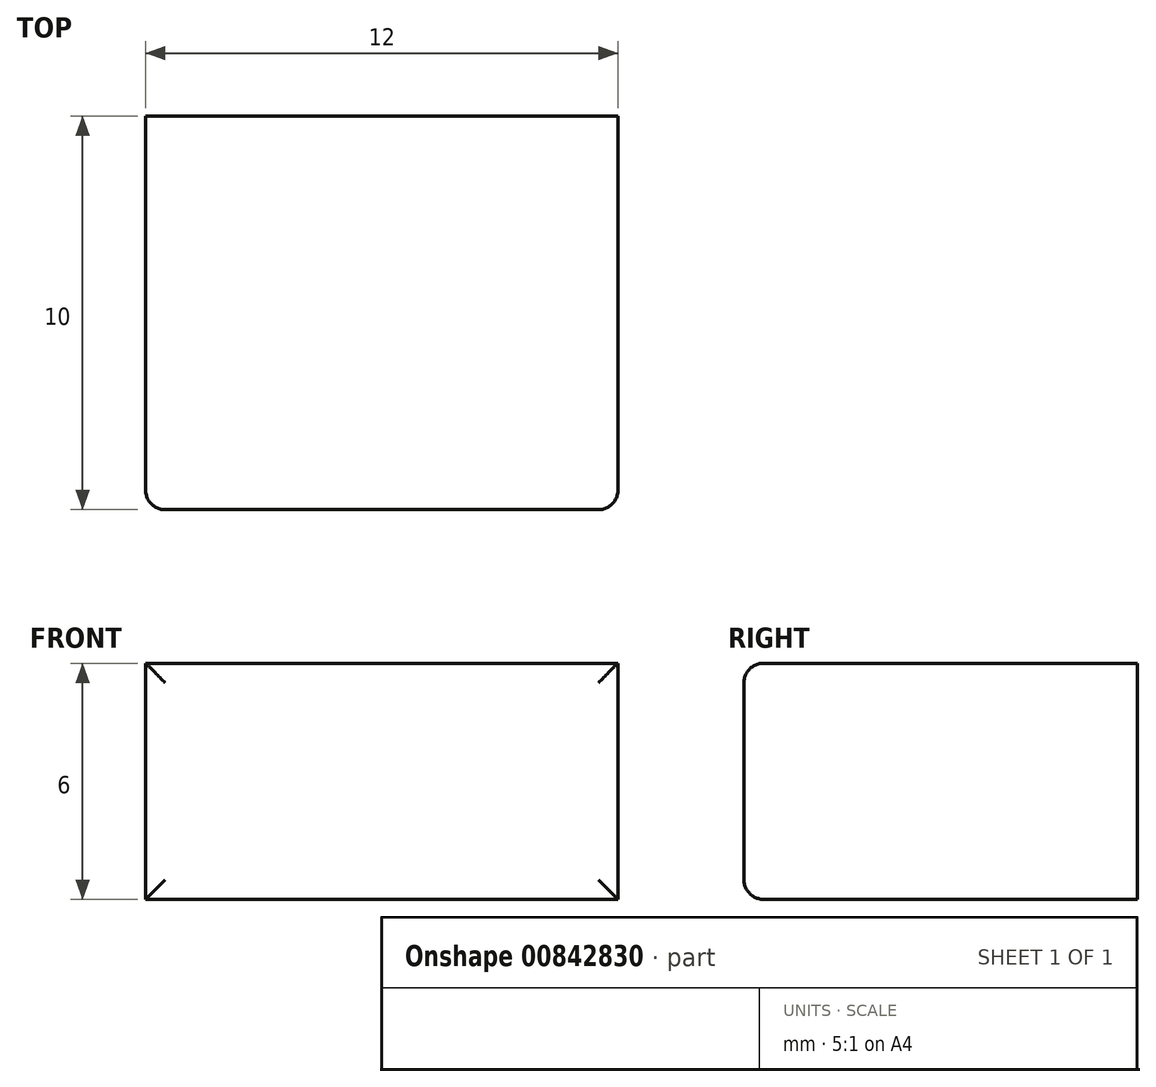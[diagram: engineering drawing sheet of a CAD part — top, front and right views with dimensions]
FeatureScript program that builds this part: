
annotation { "Feature Type Name" : "Feature", "Feature Type Description" : "" }
export const myFeature = defineFeature(function(context is Context, id is Id, definition is map)
    precondition{}
    {
        {
            var Q0;
            Q0=qCreatedBy(makeId("Front.planeOp"),FACE);
            var sketch = newSketch(context, id + "F0", { "sketchPlane" : qUnion([Q0])});
            skLineSegment(sketch, "E0.bottom", {"start": v(6, -3) * mm, "end": v(-6, -3) * mm});
            skLineSegment(sketch, "E0.top", {"start": v(6, 3) * mm, "end": v(-6, 3) * mm});
            skLineSegment(sketch, "E0.left", {"start": v(6, -3) * mm, "end": v(6, 3) * mm});
            skLineSegment(sketch, "E0.right", {"start": v(-6, -3) * mm, "end": v(-6, 3) * mm});
            skPoint(sketch, "E0.middle", {"position": v(0, 0) * mm});
            skSolve(sketch);
        }
        {
            var Q0;
            Q0=makeQuery(id+"F0.imprint","IMPRINT",FACE,{"disambiguationData":[TD([[makeQuery(id+"F0.imprint","IMPRINT",EDGE,{"derivedFrom":sQuery(id+"F0.wireOp",EDGE,"E0.bottom")}),-1.0]])]});
            extrude(context, id + "F1", {"entities" : qUnion([Q0]), "depth" : 10 * mm, "offsetDistance" : 25 * mm});
        }
        {
            var Q0;
            Q0=makeQuery(id+"F1.opExtrude","CAP_EDGE",EDGE,{"disambiguationData":[OSD([sQuery(id+"F0.wireOp",EDGE,"E0.top")])],"isStart":false});
            var Q1;
            Q1=makeQuery(id+"F1.opExtrude","CAP_EDGE",EDGE,{"disambiguationData":[OSD([sQuery(id+"F0.wireOp",EDGE,"E0.right")])],"isStart":false});
            var Q2;
            Q2=makeQuery(id+"F1.opExtrude","CAP_EDGE",EDGE,{"disambiguationData":[OSD([sQuery(id+"F0.wireOp",EDGE,"E0.left")])],"isStart":false});
            var Q3;
            Q3=makeQuery(id+"F1.opExtrude","CAP_EDGE",EDGE,{"disambiguationData":[OSD([sQuery(id+"F0.wireOp",EDGE,"E0.bottom")])],"isStart":false});
            fillet(context, id + "F2", {"entities" : qUnion([Q0, Q1, Q2, Q3]), "radius" : .5 * mm, "tangentPropagation" : true, "allowEdgeOverflow" : false});
        }
    });
